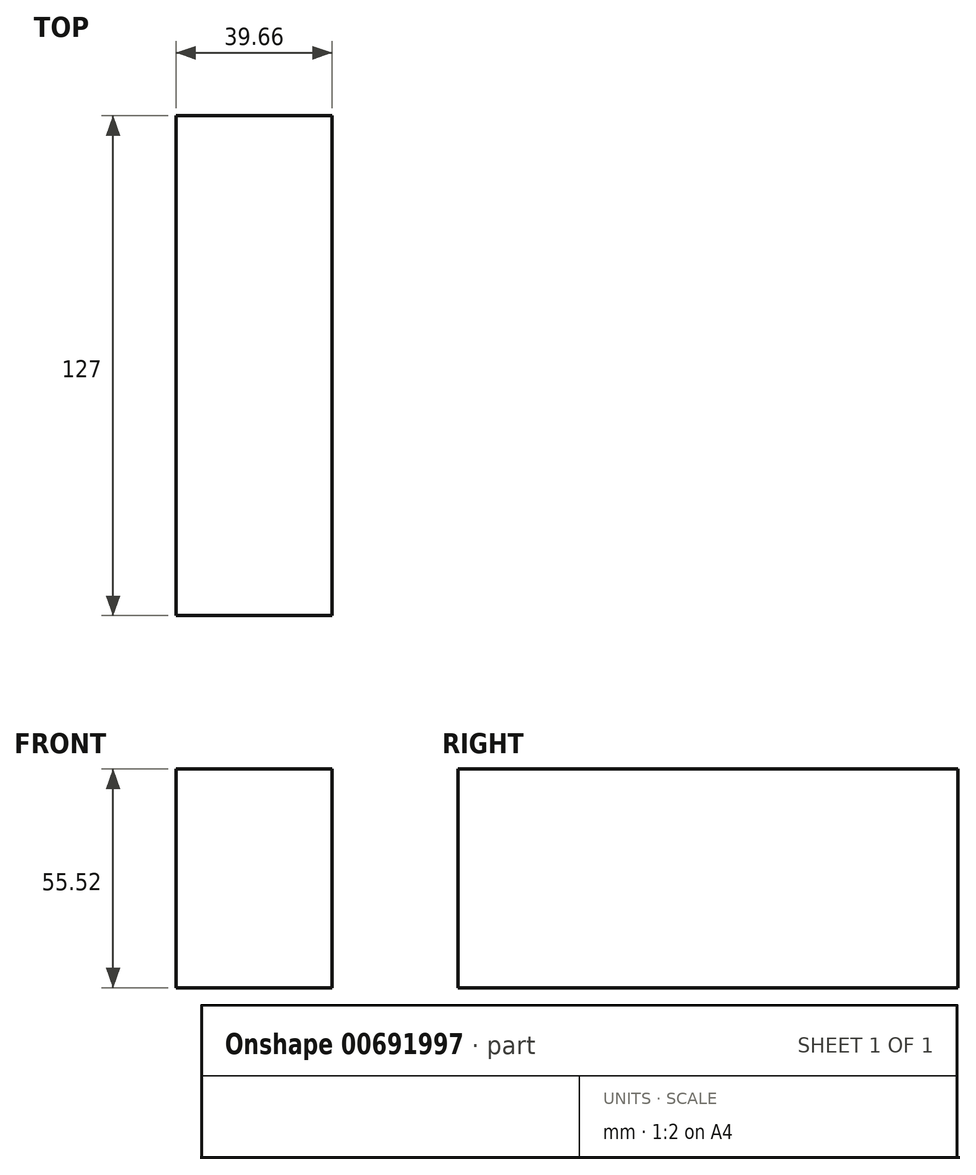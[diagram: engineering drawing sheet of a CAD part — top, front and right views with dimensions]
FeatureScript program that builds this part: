
annotation { "Feature Type Name" : "Feature", "Feature Type Description" : "" }
export const myFeature = defineFeature(function(context is Context, id is Id, definition is map)
    precondition{}
    {
        {
            var Q0;
            Q0=qCreatedBy(makeId("Front.planeOp"),FACE);
            var sketch = newSketch(context, id + "F0", { "sketchPlane" : qUnion([Q0])});
            skLineSegment(sketch, "E0.bottom", {"start": v(19.83, 27.76) * mm, "end": v(-19.83, 27.76) * mm});
            skLineSegment(sketch, "E0.top", {"start": v(19.83, -27.76) * mm, "end": v(-19.83, -27.76) * mm});
            skLineSegment(sketch, "E0.left", {"start": v(19.83, 27.76) * mm, "end": v(19.83, -27.76) * mm});
            skLineSegment(sketch, "E0.right", {"start": v(-19.83, 27.76) * mm, "end": v(-19.83, -27.76) * mm});
            skPoint(sketch, "E0.middle", {"position": v(0, 0) * mm});
            skSolve(sketch);
        }
        {
            var Q0;
            Q0=makeQuery(id+"F0.imprint","IMPRINT",FACE,{"disambiguationData":[TD([[makeQuery(id+"F0.imprint","IMPRINT",EDGE,{"derivedFrom":sQuery(id+"F0.wireOp",EDGE,"E0.bottom")}),1.0]])]});
            extrude(context, id + "F1", {"entities" : qUnion([Q0]), "depth" : 127 * mm, "offsetDistance" : 25.4 * mm});
        }
    });
